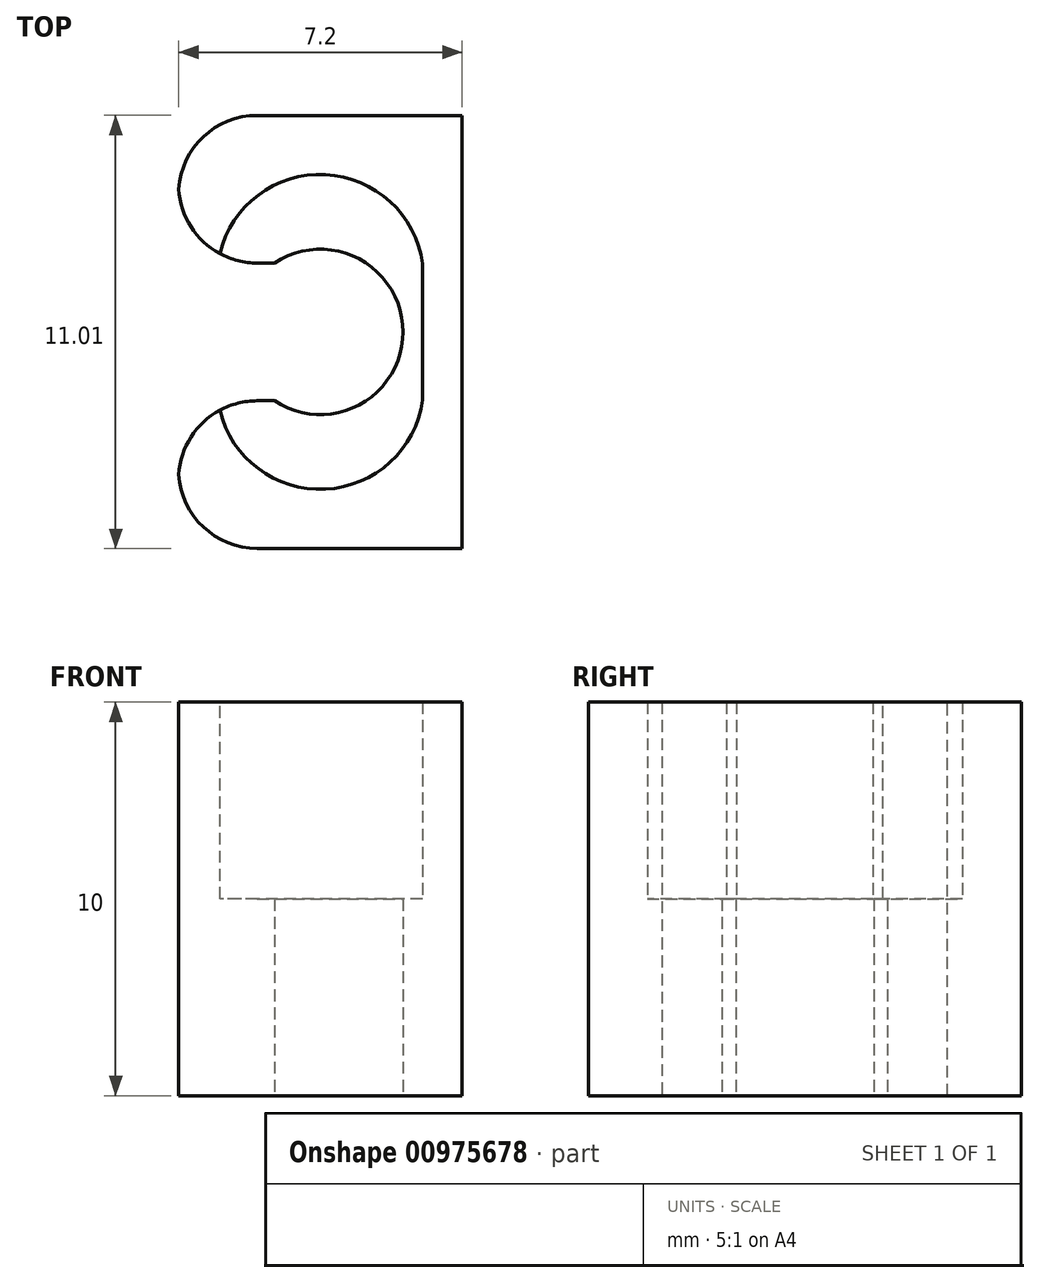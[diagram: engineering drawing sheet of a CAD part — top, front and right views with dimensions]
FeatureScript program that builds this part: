
annotation { "Feature Type Name" : "Feature", "Feature Type Description" : "" }
export const myFeature = defineFeature(function(context is Context, id is Id, definition is map)
    precondition{}
    {
        {
            var Q0;
            Q0=qCreatedBy(makeId("Top.planeOp"),FACE);
            var sketch = newSketch(context, id + "F0", { "sketchPlane" : qUnion([Q0])});
            skArc(sketch, "E0", {"start": v(2.36, 2) * mm, "mid": v(-0.24, 4.27) * mm, "end": v(-2.84, 2) * mm});
            skArc(sketch, "E1.MirrorCS", {"start": v(2.36, -1.47) * mm, "mid": v(-0.24, -3.74) * mm, "end": v(-2.84, -1.47) * mm});
            skLineSegment(sketch, "E2", {"start": v(2.36, 2) * mm, "end": v(2.36, -1.47) * mm});
            skLineSegment(sketch, "E3", {"start": v(-2.84, -1.47) * mm, "end": v(-2.84, 2) * mm});
            skLineSegment(sketch, "E4.bottom", {"start": v(3.36, -5.24) * mm, "end": v(-3.84, -5.24) * mm});
            skLineSegment(sketch, "E4.top", {"start": v(3.36, 5.77) * mm, "end": v(-3.84, 5.77) * mm});
            skLineSegment(sketch, "E4.left", {"start": v(3.36, -5.24) * mm, "end": v(3.36, 5.77) * mm});
            skLineSegment(sketch, "E4.right", {"start": v(-3.84, -5.24) * mm, "end": v(-3.84, 5.77) * mm});
            skPoint(sketch, "E5", {"position": v(3.36, 0.27) * mm});
            skPoint(sketch, "E6", {"position": v(-2.84, 0.27) * mm});
            skLineSegment(sketch, "E7", {"start": v(46.53, 0.27) * mm, "end": v(-20.53, 0.27) * mm, "construction": true});
            skPoint(sketch, "E7.startSnap0", {"position": v(-3.84, 0.27) * mm});
            skLineSegment(sketch, "E8", {"start": v(-0.24, -6.74) * mm, "end": v(-0.24, -6.82) * mm, "construction": true});
            skPoint(sketch, "E8.startSnap0", {"position": v(-0.24, 5.77) * mm});
            skPoint(sketch, "E8.endSnap0", {"position": v(-0.24, -5.24) * mm});
            skPoint(sketch, "E9", {"position": v(-0.24, 0.27) * mm});
            skCircle(sketch, "E10", {"center": v(-0.24, 0.27) * mm, "radius": 2.1 * mm});
            skLineSegment(sketch, "E11", {"start": v(-0.24, 8.2) * mm, "end": v(-0.24, -6.3) * mm, "construction": true});
            skLineSegment(sketch, "E12", {"start": v(-7.45, 2.02) * mm, "end": v(3.36, 2.02) * mm, "construction": true});
            skLineSegment(sketch, "E13.MirrorCS", {"start": v(-7.45, -1.48) * mm, "end": v(3.36, -1.48) * mm, "construction": true});
            skLineSegment(sketch, "E14", {"start": v(-3.84, 2.02) * mm, "end": v(-1.4, 2.02) * mm});
            skLineSegment(sketch, "E15", {"start": v(-3.84, -1.48) * mm, "end": v(-1.4, -1.48) * mm});
            skSolve(sketch);
        }
        {
            var Q0;
            {var subQ1=sQuery(id+"F0.wireOp",EDGE,"E2");Q0=makeQuery(id+"F0.imprint","IMPRINT",FACE,{"disambiguationData":[TD([[makeQuery(id+"F0.imprint","IMPRINT",EDGE,{"derivedFrom":subQ1}),1.0]])]});}
            extrude(context, id + "F1", {"entities" : qUnion([Q0]), "depth" : 10 * mm, "offsetDistance" : 25 * mm});
        }
        {
            var Q0;
            {var subQ5=sQuery(id+"F0.wireOp",EDGE,"E2");Q0=makeQuery(id+"F0.imprint","IMPRINT",FACE,{"disambiguationData":[TD([[makeQuery(id+"F0.imprint","IMPRINT",EDGE,{"derivedFrom":subQ5}),-1.0]])]});}
            extrude(context, id + "F2", {"entities" : qUnion([Q0]), "operationType" : NewBodyOperationType.ADD, "depth" : 5 * mm, "offsetDistance" : 25 * mm});
        }
        {
            var Q0;
            Q0=makeQuery(id+"F1.opExtrude","SWEPT_EDGE",EDGE,{"disambiguationData":[OSD([sQuery(id+"F0.wireOp",EDGE,"E4.right"),sQuery(id+"F0.wireOp",EDGE,"E14")])]});
            var Q1;
            Q1=makeQuery(id+"F1.opExtrude","SWEPT_EDGE",EDGE,{"disambiguationData":[OSD([sQuery(id+"F0.wireOp",EDGE,"E4.right"),sQuery(id+"F0.wireOp",EDGE,"E15")])]});
            var Q2;
            Q2=makeQuery(id+"F1.opExtrude","SWEPT_EDGE",EDGE,{"disambiguationData":[OSD([sQuery(id+"F0.wireOp",EDGE,"E4.bottom"),sQuery(id+"F0.wireOp",EDGE,"E4.right")])]});
            var Q3;
            Q3=makeQuery(id+"F1.opExtrude","SWEPT_EDGE",EDGE,{"disambiguationData":[OSD([sQuery(id+"F0.wireOp",EDGE,"E4.top"),sQuery(id+"F0.wireOp",EDGE,"E4.right")])]});
            fillet(context, id + "F3", {"entities" : qUnion([Q0, Q1, Q2, Q3]), "tangentPropagation" : true, "radius" : 2 * mm, "defaultsChanged" : false, "vertexSettings" : [], "allowEdgeOverflow" : false});
        }
    });
